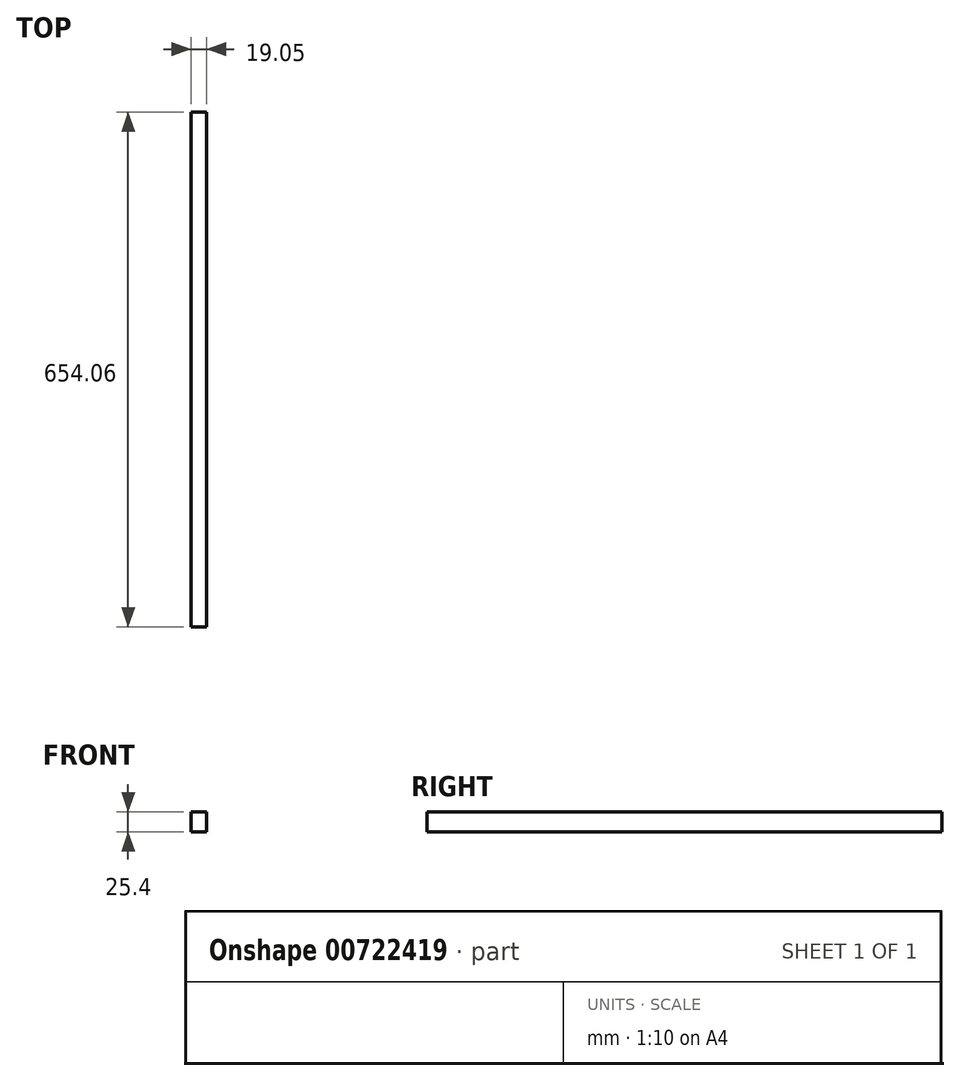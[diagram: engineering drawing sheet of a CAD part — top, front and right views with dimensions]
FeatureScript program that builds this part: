
annotation { "Feature Type Name" : "Feature", "Feature Type Description" : "" }
export const myFeature = defineFeature(function(context is Context, id is Id, definition is map)
    precondition{}
    {
        {
            var Q0;
            Q0=qCreatedBy(makeId("Right.planeOp"),FACE);
            var sketch = newSketch(context, id + "F0", { "sketchPlane" : qUnion([Q0])});
            skLineSegment(sketch, "E0.bottom", {"start": v(327.03, -12.7) * mm, "end": v(-327.03, -12.7) * mm});
            skLineSegment(sketch, "E0.top", {"start": v(327.03, 12.7) * mm, "end": v(-327.03, 12.7) * mm});
            skLineSegment(sketch, "E0.left", {"start": v(327.03, -12.7) * mm, "end": v(327.03, 12.7) * mm});
            skLineSegment(sketch, "E0.right", {"start": v(-327.03, -12.7) * mm, "end": v(-327.03, 12.7) * mm});
            skPoint(sketch, "E0.middle", {"position": v(0, 0) * mm});
            skSolve(sketch);
        }
        {
            var Q0;
            Q0=makeQuery(id+"F0.imprint","IMPRINT",FACE,{"disambiguationData":[TD([[makeQuery(id+"F0.imprint","IMPRINT",EDGE,{"derivedFrom":sQuery(id+"F0.wireOp",EDGE,"E0.bottom")}),-1.0]])]});
            extrude(context, id + "F1", {"entities" : qUnion([Q0]), "depth" : 19.05 * mm, "offsetDistance" : 25.4 * mm});
        }
    });
